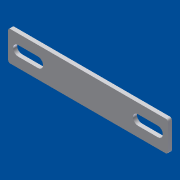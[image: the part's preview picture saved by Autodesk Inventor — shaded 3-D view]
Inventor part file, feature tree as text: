
AUTODESK INVENTOR PART (.ipt)
format: ipt  version: 2012 SP1 (Build 160190100, 190)  size: 104,448 bytes
history: native  units: in
note: dims shown in document units (in); Inventor stores cm internally (conversion verified against a paired STEP export)
features: extrude x2, sketch x2, fillet x1
ambient origin geometry x8: Origin, YZ Plane, XZ Plane, XY Plane, X Axis, Y Axis, Z Axis, Center Point
bodies: Solid1 (feature_tree)
feature tree (5):
  extrude  "Extrusion1"  Depth=0.5906in
  extrude  "Extrusion2"  Depth=0.2953in
  fillet  "Fillet1"  Radius=0.0787in
  sketch  "Sketch1"  dims[d0=3.1496in d1=0.5906in]
  sketch  "Sketch2"  dims[d2=1.5748in d3=0.2953in d4=0.0787in d5=0.0in d6=0.1969in d7=0.1969in d8=0.3937in d9=0.1969in d10=0.2953in d11=0.2953in d12=0.1969in d13=0.7874in d15=2.3622in d16=0.3937in d18=0.3937in d20=0.1181in d21=0.0in d22=0.0394in]
